# Revit family: Deca_Acionamento monocomando de mesa para cozinha_Deca You_4992.99.03
name_source: partatom
category: Plumbing Fixtures
units: mm (PartAtom-declared; Revit-internal decimal feet)

## family parameters
Cut with Voids When Loaded = No
Host = Face
Part Type = Normal
Room Calculation Point = No
Round Connector Dimension = Use Diameter
Shared = Yes

## types (5) — shared parameters
Aprovado por = quattroD
Atendimento ao Cliente = 0800-0117073
Categoria = METAIS PARA COZINHA
Composição Anel Vedação = -
Composição Assento = -
Composição Componente = -
Consumo = -
Cor Interna = -
Cor Secundária = -
Cores Componente = -
Criado por = quattroD
Código Pai = 4992.99.03
Description = Acionamento monocomando de mesa para cozinha
Informações Complementares = -
Itens de Instalação = -
Linha = Deca You
Manufacturer = Deca
Norma = Não Possui
Peso Líquido (Kg) = 0.779
Pressão máx. funcionamento = 40 MCA
Pressão mín. Aquec. Acúmulo = 10 MCA
Pressão mín. Aquec. Passagem = 10 MCA
Pressão mín. funcionamento = 10 MCA
Saída de Esgoto = -
Segmento = Banheiro Luxo
Tipo de dispositivo economizador = Não
Tipo de mecanismo utilizado = Cartucho Monocomando
Tipo de rosca de entrada = BSP NBR 8133
Tipo de rosca de saída = -
URL = www.deca.com.br
Vazão na Pressão máx. (L/min) = 9
Vazão na Pressão mín. (L/min) = 4
zero-valued in all types: Default Elevation

## per-type parameters (varying)
| type | Acompanha o Produto | Composição Básica | Cor Principal | Material | Model |
| 4992.BL99.MT.03_Black Matte | - | Liga de cobre (bronze e latão), elastômeros e plásticos de engenharia. | Black Matte | Deca_Black Matte | 4992.BL99.MT.03 |
| 4992.C99.03_Cromado | - | Liga de Cobre (bronze e latão),Plásticos de Engenharia,Elastômeros | Cromado | Deca_Cromado | 4992.C99.03 |
| 4992.CT99.MT.03_Corten | - | Liga de cobre (bronze e latão), elastômeros e plásticos de engenharia. | Corten | Deca_Corten | 4992.CT99.MT.03 |
| 4992.GL99.RD.03_Red Gold | - | Liga de cobre (bronze e latão), elastômeros e plásticos de engenharia. | Red Gold | Deca_Red Gold | 4992.GL99.RD.03 |
| 4992.INX99.03_Inox | Acompanha Ligação Flexivel | Liga de cobre (bronze e latão), elastômeros e plásticos de engenharia. | Inox | Deca_Inox | 4992.INX99.03 |

note: source unit labels omitted for Vazão na Pressão máx. (L/min), Vazão na Pressão mín. (L/min) — the stored unit's dimension contradicts the parameter name (converter mislabeling)

## geometry (parser evidence)
native form markers: Sweep x2
no freeform markers — native parametric forms only
